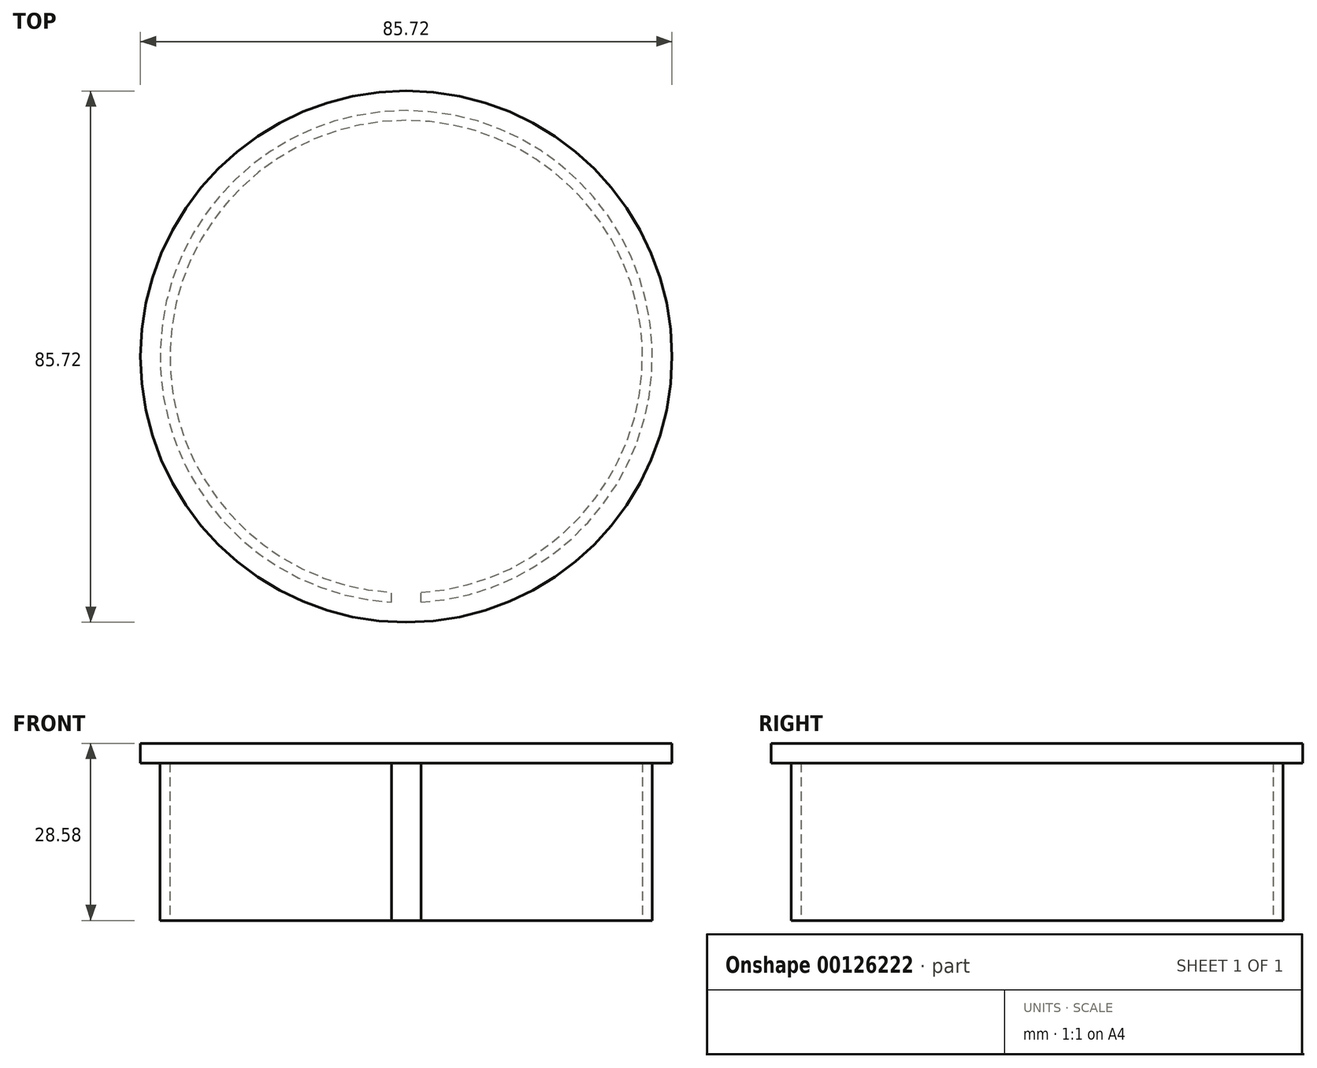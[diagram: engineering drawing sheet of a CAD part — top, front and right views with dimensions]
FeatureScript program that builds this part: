
annotation { "Feature Type Name" : "Feature", "Feature Type Description" : "" }
export const myFeature = defineFeature(function(context is Context, id is Id, definition is map)
    precondition{}
    {
        {
            var Q0;
            Q0=qCreatedBy(makeId("Front.planeOp"),FACE);
            var sketch = newSketch(context, id + "F0", { "sketchPlane" : qUnion([Q0])});
            skLineSegment(sketch, "E0", {"start": v(-38.1, 0) * mm, "end": v(-39.69, 0) * mm});
            skLineSegment(sketch, "E1", {"start": v(-39.69, 0) * mm, "end": v(-39.69, 25.4) * mm});
            skLineSegment(sketch, "E2", {"start": v(-42.86, 28.58) * mm, "end": v(0, 28.58) * mm});
            skLineSegment(sketch, "E3", {"start": v(0, 28.58) * mm, "end": v(0, 25.4) * mm});
            skLineSegment(sketch, "E4", {"start": v(0, 25.4) * mm, "end": v(-38.1, 25.4) * mm});
            skLineSegment(sketch, "E5", {"start": v(-38.1, 25.4) * mm, "end": v(-38.1, 0) * mm});
            skLineSegment(sketch, "E6", {"start": v(-42.86, 28.58) * mm, "end": v(-42.86, 25.4) * mm});
            skLineSegment(sketch, "E7", {"start": v(-42.86, 25.4) * mm, "end": v(-39.69, 25.4) * mm});
            skLineSegment(sketch, "E8", {"start": v(0, 0) * mm, "end": v(0, 28.58) * mm, "construction": true});
            skSolve(sketch);
        }
        {
            var Q0;
            Q0 = qSketchRegion(id + "F0", true);
            var Q1;
            Q1=sQuery(id+"F0.wireOp",EDGE,"E8");
            revolve(context, id + "F1", {"entities" : qUnion([Q0]), "axis" : qUnion([Q1]), "revolveType" : RevolveType.FULL});
        }
        {
            var Q0;
            Q0=qCreatedBy(makeId("Front.planeOp"),FACE);
            var sketch = newSketch(context, id + "F2", { "sketchPlane" : qUnion([Q0])});
            skLineSegment(sketch, "E9.bottom", {"start": v(-2.38, 25.4) * mm, "end": v(2.38, 25.4) * mm});
            skLineSegment(sketch, "E9.top", {"start": v(-2.38, 0) * mm, "end": v(2.38, 0) * mm});
            skLineSegment(sketch, "E9.left", {"start": v(-2.38, 25.4) * mm, "end": v(-2.38, 0) * mm});
            skLineSegment(sketch, "E9.right", {"start": v(2.38, 25.4) * mm, "end": v(2.38, 0) * mm});
            skSolve(sketch);
        }
        {
            var Q0;
            Q0 = qSketchRegion(id + "F2", true);
            var Q1;
            Q1=makeQuery(id+"F1.opRevolve","SWEPT_BODY",BODY,{"disambiguationData":[OSD([sQuery(id+"F0.wireOp",EDGE,"E0"),sQuery(id+"F0.wireOp",EDGE,"E1"),sQuery(id+"F0.wireOp",EDGE,"E2"),sQuery(id+"F0.wireOp",EDGE,"E3"),sQuery(id+"F0.wireOp",EDGE,"E4"),sQuery(id+"F0.wireOp",EDGE,"E5"),sQuery(id+"F0.wireOp",EDGE,"E6"),sQuery(id+"F0.wireOp",EDGE,"E7")])]});
            extrude(context, id + "F3", {"entities" : qUnion([Q0]), "operationType" : NewBodyOperationType.REMOVE, "endBound" : BoundingType.THROUGH_ALL, "endBoundEntityBody" : qUnion([Q1]), "depth" : 25.4 * mm});
        }
    });
